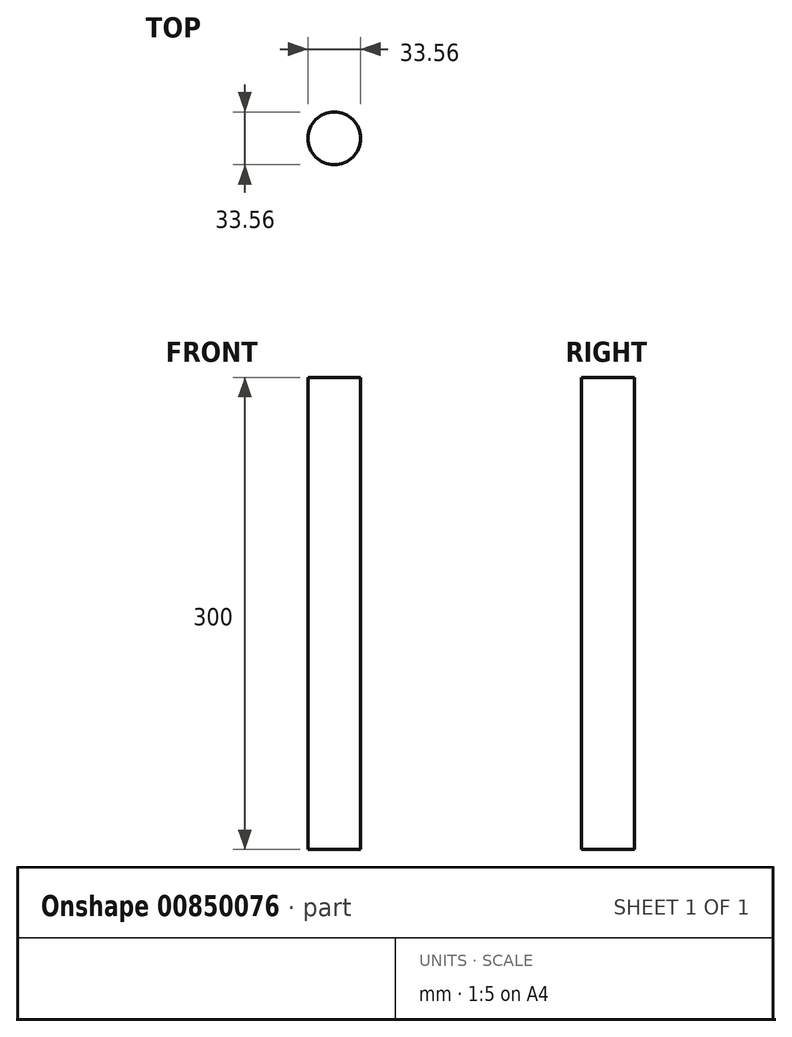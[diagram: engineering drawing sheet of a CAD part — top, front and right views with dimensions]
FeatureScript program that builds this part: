
annotation { "Feature Type Name" : "Feature", "Feature Type Description" : "" }
export const myFeature = defineFeature(function(context is Context, id is Id, definition is map)
    precondition{}
    {
        {
            var Q0;
            Q0=qCreatedBy(makeId("Top.planeOp"),FACE);
            var sketch = newSketch(context, id + "F0", { "sketchPlane" : qUnion([Q0])});
            skCircle(sketch, "E0", {"center": v(-27.52, 31.04) * mm, "radius": 16.78 * mm});
            skSolve(sketch);
        }
        {
            var Q0;
            Q0 = qSketchRegion(id + "F0", true);
            extrude(context, id + "F1", {"entities" : qUnion([Q0]), "depth" : 300 * mm, "offsetDistance" : 25 * mm});
        }
    });
